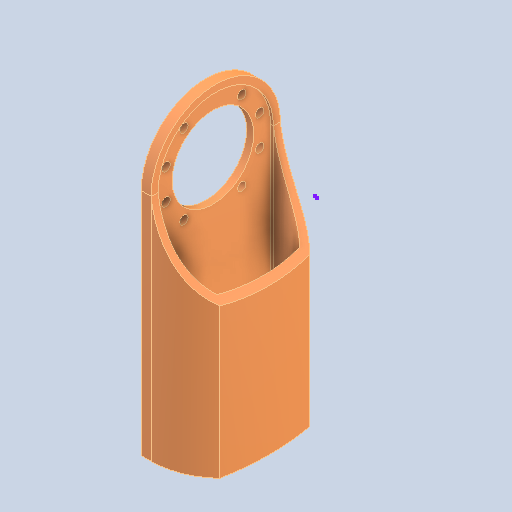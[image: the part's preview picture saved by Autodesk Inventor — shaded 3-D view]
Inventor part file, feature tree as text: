
AUTODESK INVENTOR PART (.ipt)
format: ipt  version: 2022 (Build 260153000, 153)  size: 154,112 bytes
history: native  units: in
note: dims shown in document units (in); Inventor stores cm internally (conversion verified against a paired STEP export)
features: sketch x2, other x1
ambient origin geometry x8: Origin, YZ Plane, XZ Plane, XY Plane, X Axis, Y Axis, Z Axis, Center Point
bodies: Solid2 (feature_tree), Solid1 (feature_tree)
feature tree (3):
  other  "Repaired Geometry1"
  sketch  "Sketch2"
  sketch  "Sketch4"
